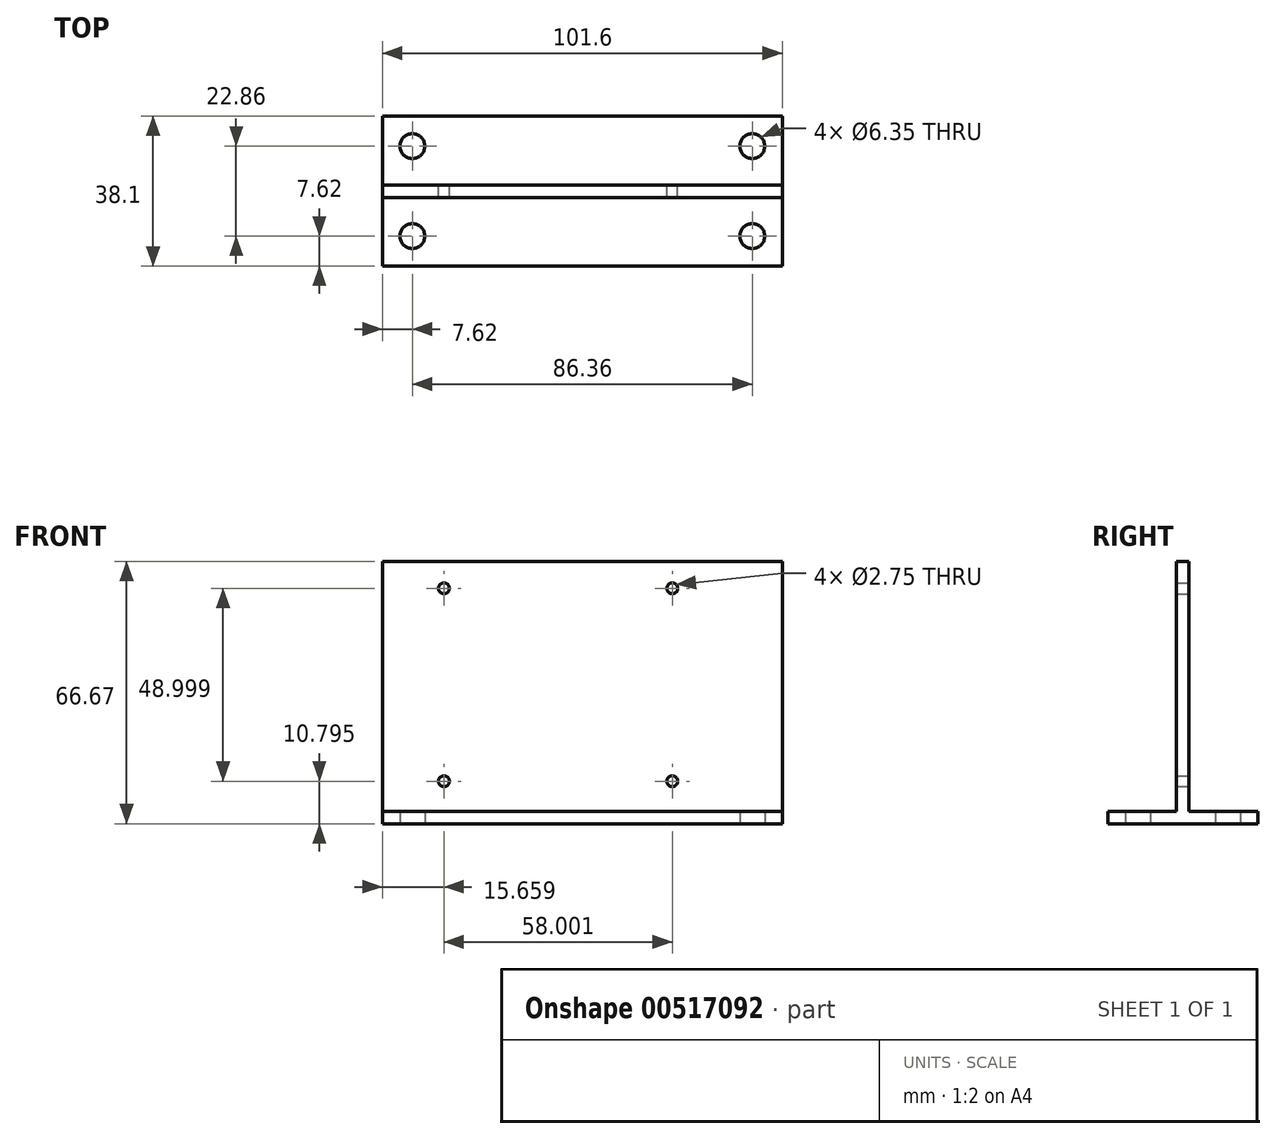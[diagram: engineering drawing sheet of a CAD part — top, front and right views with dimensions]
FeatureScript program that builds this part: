
annotation { "Feature Type Name" : "Feature", "Feature Type Description" : "" }
export const myFeature = defineFeature(function(context is Context, id is Id, definition is map)
    precondition{}
    {
        {
            var Q0;
            Q0=qCreatedBy(makeId("Top.planeOp"),FACE);
            var sketch = newSketch(context, id + "F0", { "sketchPlane" : qUnion([Q0])});
            skLineSegment(sketch, "E0.bottom", {"start": v(-50.8, 19.05) * mm, "end": v(50.8, 19.05) * mm});
            skLineSegment(sketch, "E0.top", {"start": v(-50.8, -19.05) * mm, "end": v(50.8, -19.05) * mm});
            skLineSegment(sketch, "E0.left", {"start": v(-50.8, 19.05) * mm, "end": v(-50.8, -19.05) * mm});
            skLineSegment(sketch, "E0.right", {"start": v(50.8, 19.05) * mm, "end": v(50.8, -19.05) * mm});
            skCircle(sketch, "E1", {"center": v(-43.18, 11.43) * mm, "radius": 3.18 * mm});
            skCircle(sketch, "E2", {"center": v(-43.18, -11.43) * mm, "radius": 3.18 * mm});
            skCircle(sketch, "E3", {"center": v(43.18, 11.43) * mm, "radius": 3.18 * mm});
            skCircle(sketch, "E4", {"center": v(43.18, -11.43) * mm, "radius": 3.18 * mm});
            skSolve(sketch);
        }
        {
            var Q0;
            Q0 = qSketchRegion(id + "F0", true);
            extrude(context, id + "F1", {"entities" : qUnion([Q0]), "depth" : 3.17 * mm, "offsetDistance" : 25.4 * mm});
        }
        {
            var Q0;
            Q0=qCreatedBy(makeId("Front.planeOp"),FACE);
            var sketch = newSketch(context, id + "F2", { "sketchPlane" : qUnion([Q0])});
            skLineSegment(sketch, "E5.bottom", {"start": v(-50.8, 3.18) * mm, "end": v(50.8, 3.18) * mm});
            skLineSegment(sketch, "E5.top", {"start": v(-50.8, 66.67) * mm, "end": v(50.8, 66.67) * mm});
            skLineSegment(sketch, "E5.left", {"start": v(-50.8, 3.18) * mm, "end": v(-50.8, 66.67) * mm});
            skLineSegment(sketch, "E5.right", {"start": v(50.8, 3.18) * mm, "end": v(50.8, 66.67) * mm});
            skCircle(sketch, "E6", {"center": v(22.86, 59.8) * mm, "radius": 1.38 * mm});
            skCircle(sketch, "E7", {"center": v(22.86, 10.8) * mm, "radius": 1.38 * mm});
            skCircle(sketch, "E8", {"center": v(-35.14, 59.8) * mm, "radius": 1.38 * mm});
            skCircle(sketch, "E9", {"center": v(-35.14, 10.8) * mm, "radius": 1.38 * mm});
            skSolve(sketch);
        }
        {
            var Q0;
            Q0 = qSketchRegion(id + "F2", true);
            extrude(context, id + "F3", {"entities" : qUnion([Q0]), "operationType" : NewBodyOperationType.ADD, "endBound" : BoundingType.SYMMETRIC, "depth" : 3.17 * mm, "offsetDistance" : 25.4 * mm});
        }
    });
